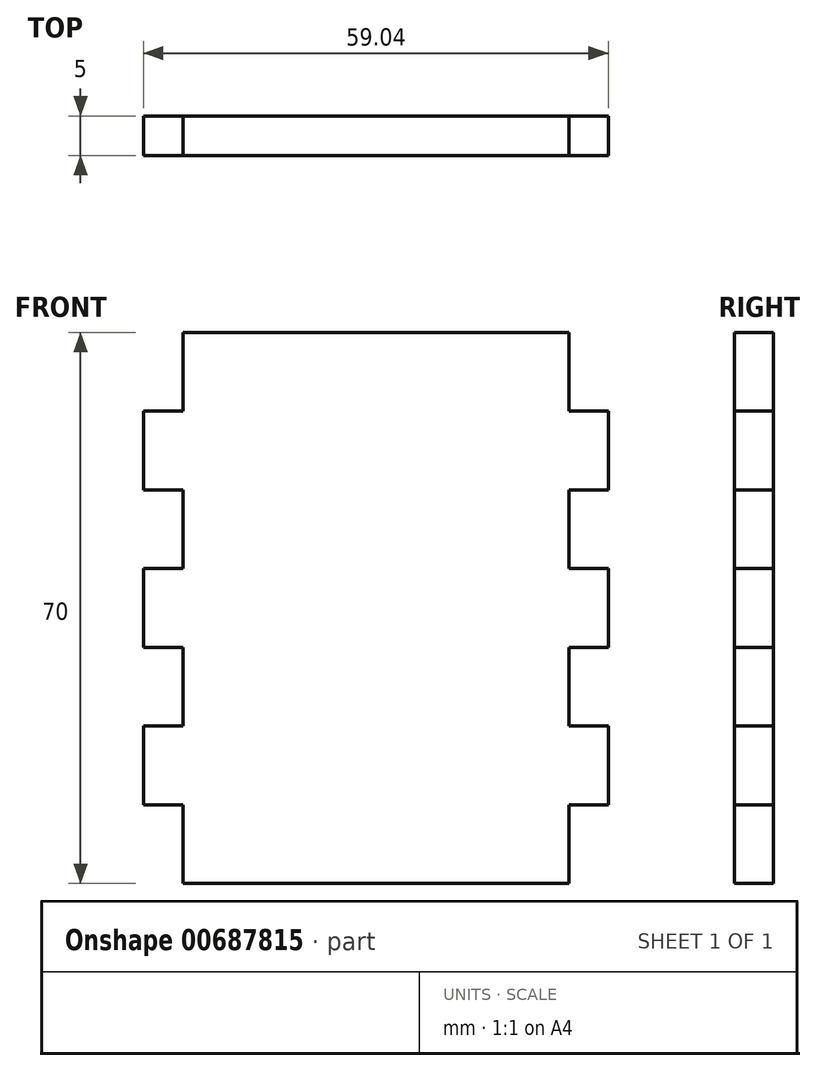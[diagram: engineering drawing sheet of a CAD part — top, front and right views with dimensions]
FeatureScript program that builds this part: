
annotation { "Feature Type Name" : "Feature", "Feature Type Description" : "" }
export const myFeature = defineFeature(function(context is Context, id is Id, definition is map)
    precondition{}
    {
        {
            var Q0;
            Q0=qCreatedBy(makeId("Front.planeOp"),FACE);
            var sketch = newSketch(context, id + "F0", { "sketchPlane" : qUnion([Q0])});
            skLineSegment(sketch, "E0.bottom", {"start": v(0, 70) * mm, "end": v(-24.52, 70) * mm});
            skLineSegment(sketch, "E0.top", {"start": v(0, 0) * mm, "end": v(-24.52, 0) * mm});
            skLineSegment(sketch, "E0.left", {"start": v(0, 70) * mm, "end": v(0, 0) * mm});
            skLineSegment(sketch, "E0.right", {"start": v(-29.52, 60) * mm, "end": v(-29.52, 50) * mm});
            skLineSegment(sketch, "E1.top", {"start": v(-29.52, 60) * mm, "end": v(-24.52, 60) * mm});
            skLineSegment(sketch, "E1.right", {"start": v(-24.52, 70) * mm, "end": v(-24.52, 60) * mm});
            skLineSegment(sketch, "E2.bottom", {"start": v(-29.52, 50) * mm, "end": v(-24.52, 50) * mm});
            skLineSegment(sketch, "E2.top", {"start": v(-29.52, 40) * mm, "end": v(-24.52, 40) * mm});
            skLineSegment(sketch, "E2.right", {"start": v(-24.52, 50) * mm, "end": v(-24.52, 40) * mm});
            skLineSegment(sketch, "E3.bottom", {"start": v(-29.52, 30) * mm, "end": v(-24.52, 30) * mm});
            skLineSegment(sketch, "E3.top", {"start": v(-29.52, 20) * mm, "end": v(-24.52, 20) * mm});
            skLineSegment(sketch, "E3.right", {"start": v(-24.52, 30) * mm, "end": v(-24.52, 20) * mm});
            skLineSegment(sketch, "E4.bottom", {"start": v(-29.52, 10) * mm, "end": v(-24.52, 10) * mm});
            skLineSegment(sketch, "E4.right", {"start": v(-24.52, 10) * mm, "end": v(-24.52, 0) * mm});
            skLineSegment(sketch, "E5.trimOffspring", {"start": v(-29.52, 40) * mm, "end": v(-29.52, 30) * mm});
            skLineSegment(sketch, "E6.trimOffspring", {"start": v(-29.52, 20) * mm, "end": v(-29.52, 10) * mm});
            skLineSegment(sketch, "E7.MirrorCS", {"start": v(24.52, 10) * mm, "end": v(24.52, 0) * mm});
            skLineSegment(sketch, "E8.MirrorCS", {"start": v(29.52, 40) * mm, "end": v(29.52, 30) * mm});
            skLineSegment(sketch, "E9.MirrorCS", {"start": v(29.52, 20) * mm, "end": v(29.52, 10) * mm});
            skLineSegment(sketch, "E10.MirrorCS", {"start": v(0, 70) * mm, "end": v(24.52, 70) * mm});
            skLineSegment(sketch, "E11.MirrorCS", {"start": v(0, 0) * mm, "end": v(24.52, 0) * mm});
            skLineSegment(sketch, "E12.MirrorCS", {"start": v(29.52, 10) * mm, "end": v(24.52, 10) * mm});
            skLineSegment(sketch, "E13.MirrorCS", {"start": v(24.52, 30) * mm, "end": v(24.52, 20) * mm});
            skLineSegment(sketch, "E14.MirrorCS", {"start": v(29.52, 20) * mm, "end": v(24.52, 20) * mm});
            skLineSegment(sketch, "E15.MirrorCS", {"start": v(29.52, 60) * mm, "end": v(29.52, 50) * mm});
            skLineSegment(sketch, "E16.MirrorCS", {"start": v(29.52, 60) * mm, "end": v(24.52, 60) * mm});
            skLineSegment(sketch, "E17.MirrorCS", {"start": v(24.52, 70) * mm, "end": v(24.52, 60) * mm});
            skLineSegment(sketch, "E18.MirrorCS", {"start": v(29.52, 30) * mm, "end": v(24.52, 30) * mm});
            skLineSegment(sketch, "E19.MirrorCS", {"start": v(24.52, 50) * mm, "end": v(24.52, 40) * mm});
            skLineSegment(sketch, "E20.MirrorCS", {"start": v(29.52, 40) * mm, "end": v(24.52, 40) * mm});
            skLineSegment(sketch, "E21.MirrorCS", {"start": v(29.52, 50) * mm, "end": v(24.52, 50) * mm});
            skSolve(sketch);
        }
        {
            var Q0;
            Q0 = qSketchRegion(id + "F0", true);
            extrude(context, id + "F1", {"entities" : qUnion([Q0]), "depth" : 5 * mm, "offsetDistance" : 25 * mm});
        }
    });
